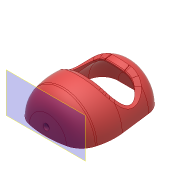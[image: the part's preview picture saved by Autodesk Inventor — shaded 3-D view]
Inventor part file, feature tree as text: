
AUTODESK INVENTOR PART (.ipt)
format: ipt  version: 2017 (Build 210142000, 142)  size: 609,792 bytes
history: native  units: mm
features: sketch x7, extrude x5, fillet x4, chamfer x3, revolve x1, shell x1, hole x1, plane x1, projected_geometry x1
ambient origin geometry x8: Origin, YZ Plane, XZ Plane, XY Plane, X Axis, Y Axis, Z Axis, Center Point
bodies: Solid1 (feature_tree)
feature tree (24):
  revolve  "Revolution1"  [1 undecoded]
  fillet  "Fillet1"  Radius=30.0mm
  chamfer  "Chamfer1"  Distance=10.0mm Angle=45.0deg
  fillet  "Fillet2"  Radius=20.0mm
  fillet  "Fillet3"  Radius=60.0mm
  extrude  "Extrusion1"  Depth=4.0mm
  shell  "Shell1"  Thickness=28.0mm
  extrude  "Extrusion2"  Depth=28.0mm
  chamfer  "Chamfer2"  Distance=100.0mm
  chamfer  "Chamfer3"  Distance=80.0mm
  extrude  "Extrusion3"  Depth=10.0mm TaperAngle=0.0deg
  extrude  "Extrusion4"  Depth=2.0mm
  hole  "Hole1"  [1 undecoded]
  plane  "Work Plane1"
  extrude  "Extrusion5"  Depth=3.0mm TaperAngle=45.0deg
  fillet  "Fillet4"  Radius=3.0mm
  sketch  "Sketch1"  dims[d0=40.0mm d1=80.0mm d2=30.0mm]
  sketch  "Sketch2"  dims[d3=90.0deg]
  sketch  "Sketch3"  dims[d4=20.0mm d5=10.0mm d6=20.0mm d7=45.0deg d8=20.0mm d9=60.0mm]
  sketch  "Sketch4"  dims[d10=10.0mm d11=0.0mm d12=4.0mm d13=28.0mm]
  sketch  "Sketch5"  dims[d14=28.0mm d15=28.0mm]
  sketch  "Sketch6"  dims[d16=46.0mm]
  projected_geometry  "Projected Loop1"
  sketch  "Sketch7"  dims[d17=13.0mm d18=100.0mm d19=0.0mm d20=80.0mm d21=10.0mm d22=0.0mm d24=120.0mm d25=80.0mm d26=3.0mm d27=2.0mm d28=45.0deg d29=3.0mm d30=2.0mm d31=45.0deg d32=6.0mm d33=12.0mm d34=14.0mm d35=0.0mm d36=8.0mm d37=24.0mm d38=4.0mm d39=0.0mm d40=8.0mm d41=3.5mm d42=6.0mm d43=4.0mm d44=2.0mm d45=90.0deg d46=8.0mm d47=20.594885mm d48=-9.5mm d49=6.0mm d50=4.0mm d51=0.0mm d52=2.0mm]
note: 2 required parameter values undecoded (feature->parameter linkage not recoverable at this tier; creation-order binding heuristic only, values carry confidence <= 0.55)